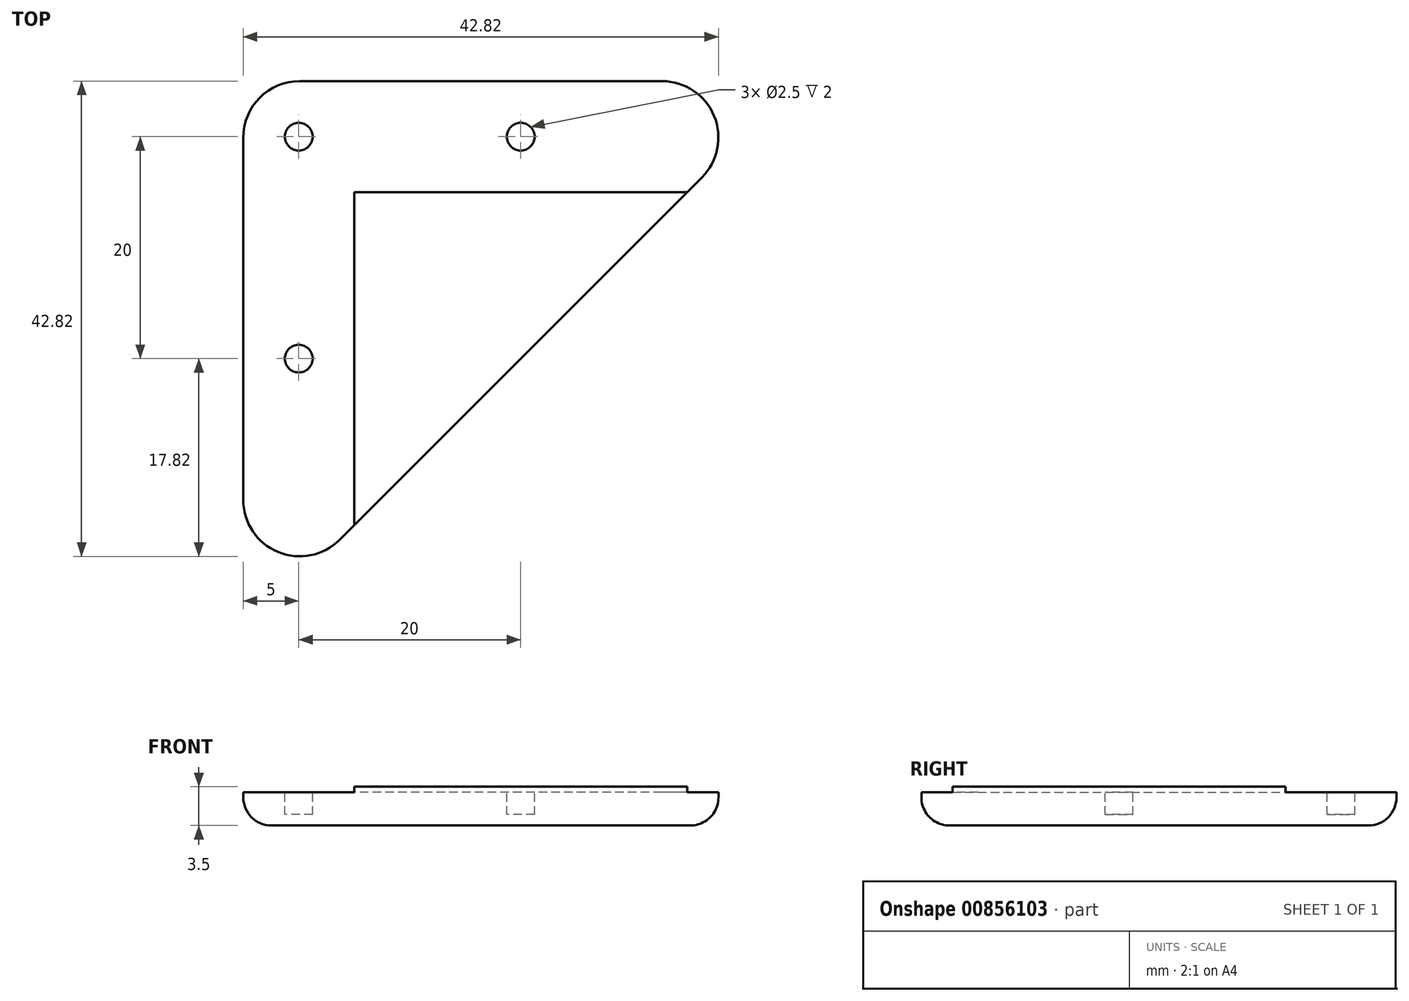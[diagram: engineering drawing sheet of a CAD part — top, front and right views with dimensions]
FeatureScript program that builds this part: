
annotation { "Feature Type Name" : "Feature", "Feature Type Description" : "" }
export const myFeature = defineFeature(function(context is Context, id is Id, definition is map)
    precondition{}
    {
        {
            var Q0;
            Q0=qCreatedBy(makeId("Top.planeOp"),FACE);
            var sketch = newSketch(context, id + "F0", { "sketchPlane" : qUnion([Q0])});
            skLineSegment(sketch, "E0.bottom", {"start": v(25, -25) * mm, "end": v(-25, -25) * mm, "construction": true});
            skLineSegment(sketch, "E0.top", {"start": v(25, 25) * mm, "end": v(-25, 25) * mm});
            skLineSegment(sketch, "E0.left", {"start": v(25, -25) * mm, "end": v(25, 25) * mm, "construction": true});
            skLineSegment(sketch, "E0.right", {"start": v(-25, -25) * mm, "end": v(-25, 25) * mm});
            skPoint(sketch, "E0.middle", {"position": v(0, 0) * mm});
            skLineSegment(sketch, "E1", {"start": v(-25, -25) * mm, "end": v(25, 25) * mm});
            skLineSegment(sketch, "E2.bottom", {"start": v(15, -15) * mm, "end": v(-15, -15) * mm, "construction": true});
            skLineSegment(sketch, "E2.top", {"start": v(15, 15) * mm, "end": v(-15, 15) * mm});
            skLineSegment(sketch, "E2.left", {"start": v(15, -15) * mm, "end": v(15, 15) * mm, "construction": true});
            skLineSegment(sketch, "E2.right", {"start": v(-15, -15) * mm, "end": v(-15, 15) * mm});
            skSolve(sketch);
        }
        {
            var Q0;
            {var subQ1=sQuery(id+"F0.wireOp",EDGE,"E0.top");Q0=makeQuery(id+"F0.imprint","IMPRINT",FACE,{"disambiguationData":[TD([[makeQuery(id+"F0.imprint","IMPRINT",EDGE,{"derivedFrom":subQ1}),1.0]])]});}
            extrude(context, id + "F1", {"entities" : qUnion([Q0]), "depth" : 3 * mm, "offsetDistance" : 25.4 * mm});
        }
        {
            var Q0;
            {var subQ0=sQuery(id+"F0.wireOp",EDGE,"E2.top");Q0=makeQuery(id+"F0.imprint","IMPRINT",FACE,{"disambiguationData":[TD([[makeQuery(id+"F0.imprint","IMPRINT",EDGE,{"derivedFrom":subQ0}),1.0]])]});}
            extrude(context, id + "F2", {"entities" : qUnion([Q0]), "operationType" : NewBodyOperationType.ADD, "depth" : 3.5 * mm, "offsetDistance" : 25.4 * mm});
        }
        {
            var Q0;
            Q0=makeQuery(id+"F1.opExtrude","CAP_FACE",FACE,{"disambiguationData":[OSD([sQuery(id+"F0.wireOp",EDGE,"E0.top"),sQuery(id+"F0.wireOp",EDGE,"E0.right"),sQuery(id+"F0.wireOp",EDGE,"E1"),sQuery(id+"F0.wireOp",EDGE,"E2.top"),sQuery(id+"F0.wireOp",EDGE,"E2.right")])],"isStart":false});
            var sketch = newSketch(context, id + "F3", { "sketchPlane" : qUnion([Q0])});
            skCircle(sketch, "E3", {"center": v(-20, 20) * mm, "radius": 1.25 * mm});
            skCircle(sketch, "E4", {"center": v(0, 20) * mm, "radius": 1.25 * mm});
            skCircle(sketch, "E5", {"center": v(-20, 0) * mm, "radius": 1.25 * mm});
            skSolve(sketch);
        }
        {
            var Q0;
            Q0=makeQuery(id+"F3.imprint","IMPRINT",FACE,{"disambiguationData":[TD([[makeQuery(id+"F3.imprint","IMPRINT",EDGE,{"derivedFrom":sQuery(id+"F3.wireOp",EDGE,"E3")}),1.0]])]});
            var Q1;
            Q1=makeQuery(id+"F3.imprint","IMPRINT",FACE,{"disambiguationData":[TD([[makeQuery(id+"F3.imprint","IMPRINT",EDGE,{"derivedFrom":sQuery(id+"F3.wireOp",EDGE,"E4")}),1.0]])]});
            var Q2;
            Q2=makeQuery(id+"F3.imprint","IMPRINT",FACE,{"disambiguationData":[TD([[makeQuery(id+"F3.imprint","IMPRINT",EDGE,{"derivedFrom":sQuery(id+"F3.wireOp",EDGE,"E5")}),1.0]])]});
            var Q3;
            Q3=sQuery(id+"F3.wireOp",EDGE,"E4");
            var Q4;
            Q4=sQuery(id+"F3.wireOp",EDGE,"E3");
            var Q5;
            Q5=sQuery(id+"F3.wireOp",EDGE,"E5");
            extrude(context, id + "F4", {"entities" : qUnion([Q0, Q1, Q2]), "operationType" : NewBodyOperationType.REMOVE, "surfaceEntities" : qUnion([Q3, Q4, Q5]), "oppositeDirection" : true, "depth" : 2 * mm, "offsetDistance" : 25.4 * mm});
        }
        {
            var Q0;
            Q0=makeQuery(id+"F1.opExtrude","SWEPT_EDGE",EDGE,{"disambiguationData":[OSD([sQuery(id+"F0.wireOp",EDGE,"E0.top"),sQuery(id+"F0.wireOp",EDGE,"E0.right")])]});
            var Q1;
            Q1=makeQuery(id+"F1.opExtrude","SWEPT_EDGE",EDGE,{"disambiguationData":[OSD([sQuery(id+"F0.wireOp",EDGE,"E0.top"),sQuery(id+"F0.wireOp",EDGE,"E1")])]});
            var Q2;
            Q2=makeQuery(id+"F1.opExtrude","SWEPT_EDGE",EDGE,{"disambiguationData":[OSD([sQuery(id+"F0.wireOp",EDGE,"E0.right"),sQuery(id+"F0.wireOp",EDGE,"E1")])]});
            fillet(context, id + "F5", {"entities" : qUnion([Q0, Q1, Q2]), "radius" : 5.08 * mm, "tangentPropagation" : true, "allowEdgeOverflow" : false});
        }
        {
            var Q0;
            {var subQ0=sQuery(id+"F0.wireOp",EDGE,"E2.right");var subQ1=sQuery(id+"F0.wireOp",EDGE,"E2.top");var subQ2=sQuery(id+"F0.wireOp",EDGE,"E1");Q0=makeQuery(id+"F2.boolean.opBoolean","MERGE",FACE,{"derivedFrom":[makeQuery(id+"F1.opExtrude","CAP_FACE",FACE,{"disambiguationData":[OSD([sQuery(id+"F0.wireOp",EDGE,"E0.top"),sQuery(id+"F0.wireOp",EDGE,"E0.right"),subQ2,subQ1,subQ0])],"isStart":true}),makeQuery(id+"F2.opExtrude","CAP_FACE",FACE,{"disambiguationData":[OSD([subQ2,subQ1,subQ0])],"isStart":true})]});}
            fillet(context, id + "F6", {"entities" : qUnion([Q0]), "radius" : 2.54 * mm, "tangentPropagation" : true, "allowEdgeOverflow" : false});
        }
    });
